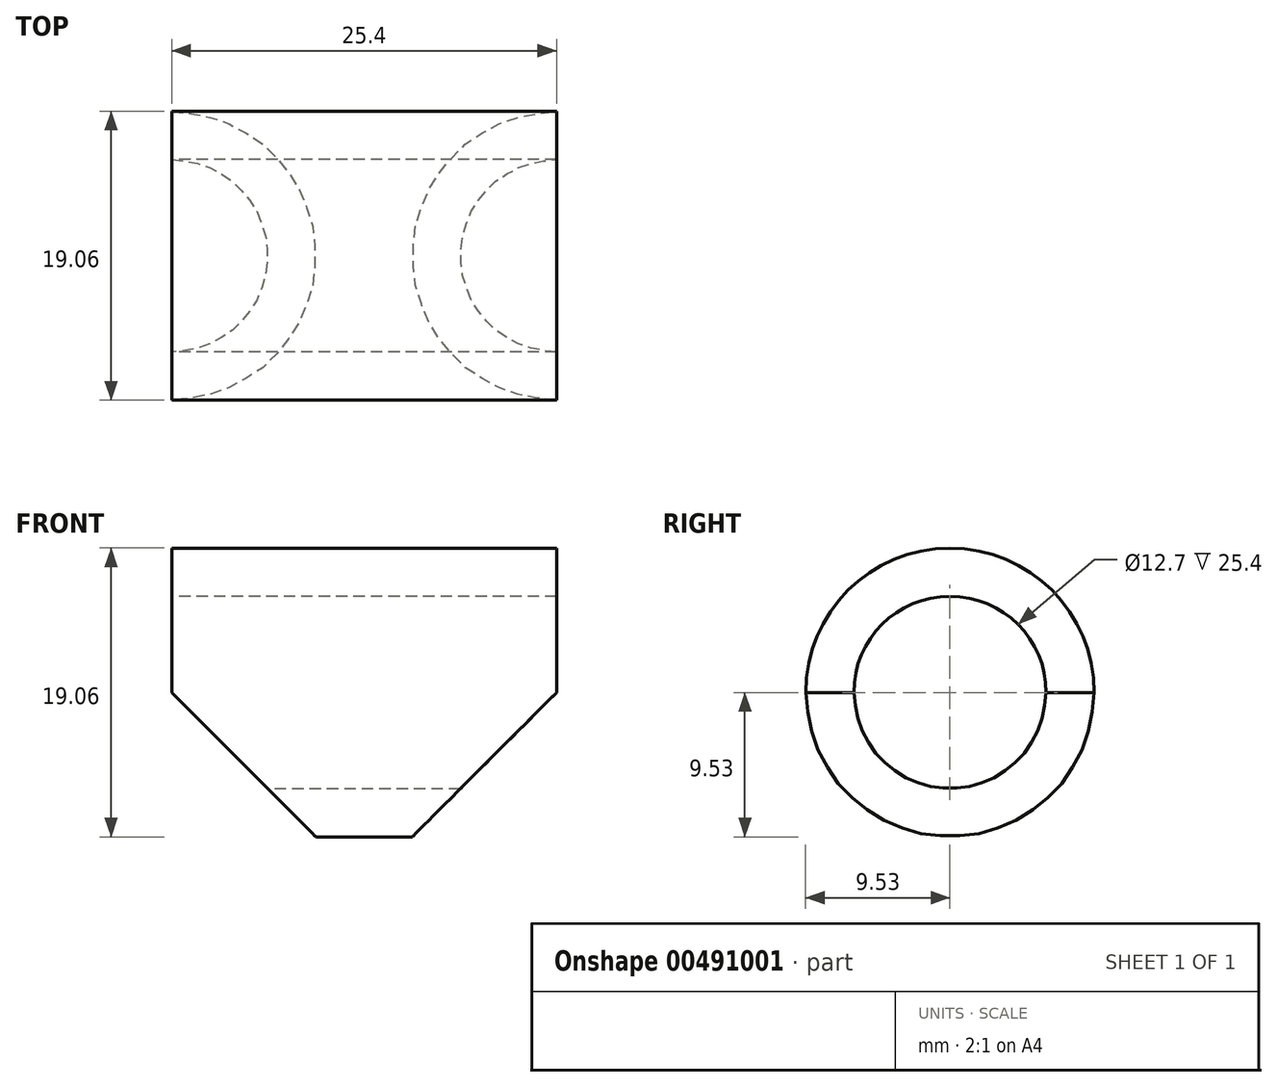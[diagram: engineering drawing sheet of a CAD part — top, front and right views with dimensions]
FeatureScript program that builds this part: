
annotation { "Feature Type Name" : "Feature", "Feature Type Description" : "" }
export const myFeature = defineFeature(function(context is Context, id is Id, definition is map)
    precondition{}
    {
        {
            var Q0;
            Q0=qCreatedBy(makeId("Right.planeOp"),FACE);
            var sketch = newSketch(context, id + "F0", { "sketchPlane" : qUnion([Q0])});
            skCircle(sketch, "E0", {"center": v(0, 0) * mm, "radius": 6.35 * mm});
            skCircle(sketch, "E1", {"center": v(0, 0) * mm, "radius": 9.53 * mm});
            skSolve(sketch);
        }
        {
            var Q0;
            Q0 = qSketchRegion(id + "F0", true);
            extrude(context, id + "F1", {"entities" : qUnion([Q0]), "endBound" : BoundingType.SYMMETRIC, "depth" : 25.4 * mm});
        }
        {
            var Q0;
            Q0=qCreatedBy(makeId("Front.planeOp"),FACE);
            var sketch = newSketch(context, id + "F2", { "sketchPlane" : qUnion([Q0])});
            skLineSegment(sketch, "E2", {"start": v(-12.7, 0) * mm, "end": v(0, -12.7) * mm});
            skLineSegment(sketch, "E3", {"start": v(0, -12.7) * mm, "end": v(12.7, 0) * mm});
            skLineSegment(sketch, "E4", {"start": v(12.7, 0) * mm, "end": v(50.38, -47.46) * mm});
            skLineSegment(sketch, "E5", {"start": v(50.38, -47.46) * mm, "end": v(-25.76, -46.1) * mm});
            skLineSegment(sketch, "E6", {"start": v(-25.76, -46.1) * mm, "end": v(-12.7, 0) * mm});
            skLineSegment(sketch, "E7", {"start": v(-12.7, 0) * mm, "end": v(12.7, 0) * mm, "construction": true});
            skLineSegment(sketch, "E8", {"start": v(-3.17, -9.52) * mm, "end": v(3.17, -9.53) * mm, "construction": true});
            skSolve(sketch);
        }
        {
            var Q0;
            Q0 = qSketchRegion(id + "F2", true);
            extrude(context, id + "F3", {"entities" : qUnion([Q0]), "operationType" : NewBodyOperationType.REMOVE, "endBound" : BoundingType.SYMMETRIC, "oppositeDirection" : true, "depth" : 25.4 * mm});
        }
    });
